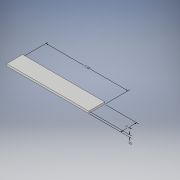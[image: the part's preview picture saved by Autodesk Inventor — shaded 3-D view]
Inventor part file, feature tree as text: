
AUTODESK INVENTOR PART (.ipt)
format: ipt  version: 2019 (Build 230136000, 136)  size: 102,400 bytes
history: native  units: in
note: dims shown in document units (in); Inventor stores cm internally (conversion verified against a paired STEP export)
features: other x4, extrude x1, sketch x1
ambient origin geometry x8: Origin, YZ Plane, XZ Plane, XY Plane, X Axis, Y Axis, Z Axis, Center Point
bodies: Solid1 (feature_tree)
feature tree (6):
  other  "Annotations"
  extrude  "Extrusion1"  Depth=1.4375in
  sketch  "Sketch1"  dims[d0=7.375in d1=1.4375in d2=0.1875in d3=0.0in d13=0.0in d14=0.3937in d15=1.4375in d16=0.0in d17=0.3937in d18=7.375in d19=0.0in d20=0.3937in d21=0.1875in]
  other  "Linear Dimension 1"
  other  "Linear Dimension 2"
  other  "Linear Dimension 3"
